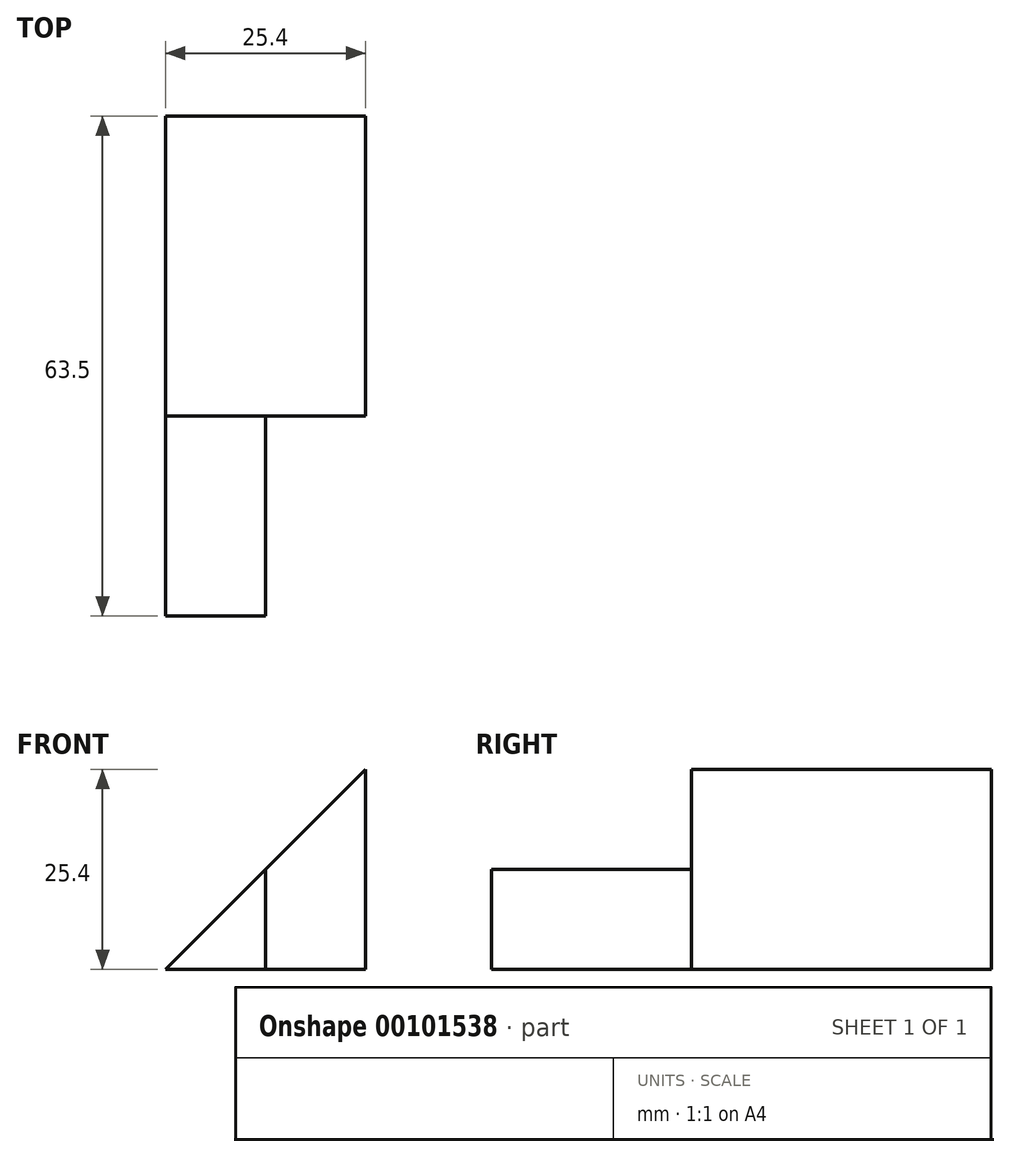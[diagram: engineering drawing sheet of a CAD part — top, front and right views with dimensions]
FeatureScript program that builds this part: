
annotation { "Feature Type Name" : "Feature", "Feature Type Description" : "" }
export const myFeature = defineFeature(function(context is Context, id is Id, definition is map)
    precondition{}
    {
        {
            var Q0;
            Q0=qCreatedBy(makeId("Front.planeOp"),FACE);
            var sketch = newSketch(context, id + "F0", { "sketchPlane" : qUnion([Q0])});
            skLineSegment(sketch, "E0", {"start": v(0, 0) * mm, "end": v(25.4, 0) * mm});
            skLineSegment(sketch, "E1", {"start": v(25.4, 0) * mm, "end": v(25.4, 25.4) * mm});
            skLineSegment(sketch, "E2", {"start": v(25.4, 25.4) * mm, "end": v(0, 0) * mm});
            skSolve(sketch);
        }
        {
            var Q0;
            Q0 = qSketchRegion(id + "F0", true);
            extrude(context, id + "F1", {"entities" : qUnion([Q0]), "depth" : 38.1 * mm});
        }
        {
            var Q0;
            Q0=makeQuery(id+"F1.opExtrude","CAP_FACE",FACE,{"disambiguationData":[OSD([sQuery(id+"F0.wireOp",EDGE,"E0"),sQuery(id+"F0.wireOp",EDGE,"E1"),sQuery(id+"F0.wireOp",EDGE,"E2")])],"isStart":false});
            var sketch = newSketch(context, id + "F2", { "sketchPlane" : qUnion([Q0])});
            skLineSegment(sketch, "E3", {"start": v(0, 0) * mm, "end": v(12.7, 0) * mm});
            skLineSegment(sketch, "E4", {"start": v(12.7, 0) * mm, "end": v(12.7, 12.7) * mm});
            skLineSegment(sketch, "E5", {"start": v(12.7, 12.7) * mm, "end": v(0, 0) * mm});
            skSolve(sketch);
        }
        {
            var Q0;
            Q0 = qSketchRegion(id + "F2", true);
            extrude(context, id + "F3", {"entities" : qUnion([Q0]), "depth" : 25.4 * mm});
        }
    });
